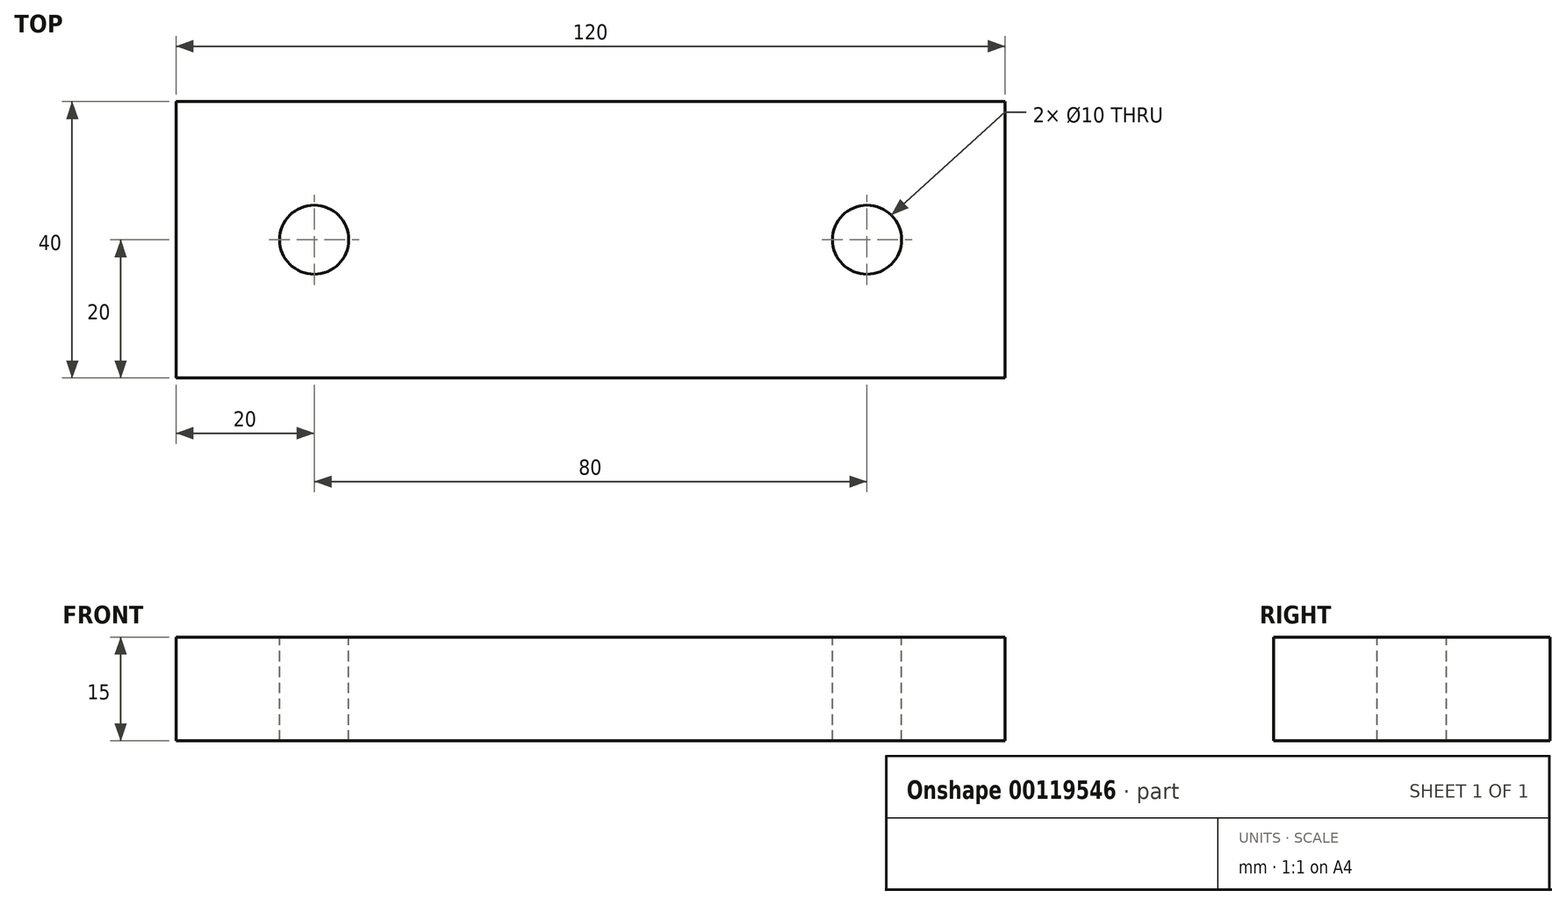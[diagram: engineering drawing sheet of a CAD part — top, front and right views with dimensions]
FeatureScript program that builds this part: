
annotation { "Feature Type Name" : "Feature", "Feature Type Description" : "" }
export const myFeature = defineFeature(function(context is Context, id is Id, definition is map)
    precondition{}
    {
        {
            var Q0;
            Q0=qCreatedBy(makeId("Front.planeOp"),FACE);
            var sketch = newSketch(context, id + "F0", { "sketchPlane" : qUnion([Q0])});
            skLineSegment(sketch, "E0.bottom", {"start": v(60, 7.5) * mm, "end": v(-60, 7.5) * mm});
            skLineSegment(sketch, "E0.top", {"start": v(60, -7.5) * mm, "end": v(-60, -7.5) * mm});
            skLineSegment(sketch, "E0.left", {"start": v(60, 7.5) * mm, "end": v(60, -7.5) * mm});
            skLineSegment(sketch, "E0.right", {"start": v(-60, 7.5) * mm, "end": v(-60, -7.5) * mm});
            skPoint(sketch, "E0.middle", {"position": v(0, 0) * mm});
            skSolve(sketch);
        }
        {
            var Q0;
            Q0 = qSketchRegion(id + "F0", true);
            extrude(context, id + "F1", {"entities" : qUnion([Q0]), "depth" : 20 * mm, "hasSecondDirection" : true, "secondDirectionOppositeDirection" : true, "secondDirectionDepth" : 20 * mm});
        }
        {
            var Q0;
            Q0=makeQuery(id+"F1.opExtrude","SWEPT_FACE",FACE,{"disambiguationData":[OSD([sQuery(id+"F0.wireOp",EDGE,"E0.bottom")])]});
            var sketch = newSketch(context, id + "F2", { "sketchPlane" : qUnion([Q0])});
            skLineSegment(sketch, "E1", {"start": v(-60, 20) * mm, "end": v(-40, 20) * mm, "construction": true});
            skLineSegment(sketch, "E2", {"start": v(-40, 20) * mm, "end": v(-40, 0) * mm, "construction": true});
            skCircle(sketch, "E3", {"center": v(-40, 0) * mm, "radius": 5 * mm});
            skCircle(sketch, "E4", {"center": v(40, 0) * mm, "radius": 5 * mm});
            skSolve(sketch);
        }
        {
            var Q0;
            Q0 = qSketchRegion(id + "F2", true);
            extrude(context, id + "F3", {"entities" : qUnion([Q0]), "operationType" : NewBodyOperationType.REMOVE, "endBound" : BoundingType.THROUGH_ALL, "oppositeDirection" : true, "depth" : 25 * mm});
        }
    });
